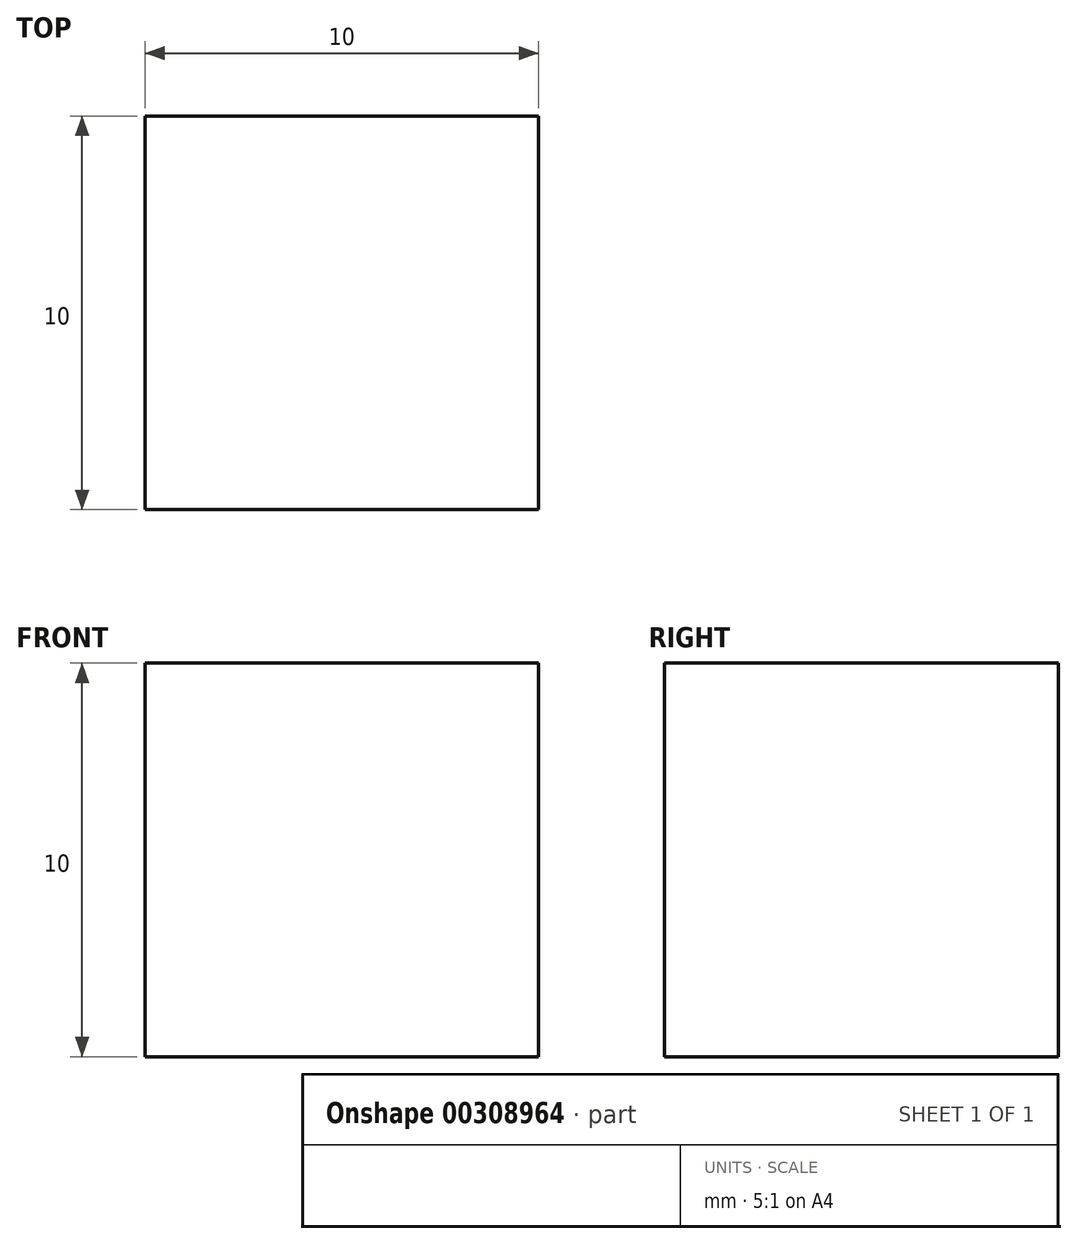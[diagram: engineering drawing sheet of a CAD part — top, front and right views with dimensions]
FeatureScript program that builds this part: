
annotation { "Feature Type Name" : "Feature", "Feature Type Description" : "" }
export const myFeature = defineFeature(function(context is Context, id is Id, definition is map)
    precondition{}
    {
        {
            var Q0;
            Q0=qCreatedBy(makeId("Front.planeOp"),FACE);
            var sketch = newSketch(context, id + "F0", { "sketchPlane" : qUnion([Q0])});
            skLineSegment(sketch, "E0.bottom", {"start": v(5, 5) * mm, "end": v(-5, 5) * mm});
            skLineSegment(sketch, "E0.top", {"start": v(5, -5) * mm, "end": v(-5, -5) * mm});
            skLineSegment(sketch, "E0.left", {"start": v(5, 5) * mm, "end": v(5, -5) * mm});
            skLineSegment(sketch, "E0.right", {"start": v(-5, 5) * mm, "end": v(-5, -5) * mm});
            skPoint(sketch, "E0.middle", {"position": v(0, 0) * mm});
            skSolve(sketch);
        }
        {
            var Q0;
            Q0=makeQuery(id+"F0.imprint","IMPRINT",FACE,{"disambiguationData":[TD([[makeQuery(id+"F0.imprint","IMPRINT",EDGE,{"derivedFrom":sQuery(id+"F0.wireOp",EDGE,"E0.bottom")}),1.0]])]});
            extrude(context, id + "F1", {"entities" : qUnion([Q0]), "endBound" : BoundingType.SYMMETRIC, "depth" : 10 * mm});
        }
    });
